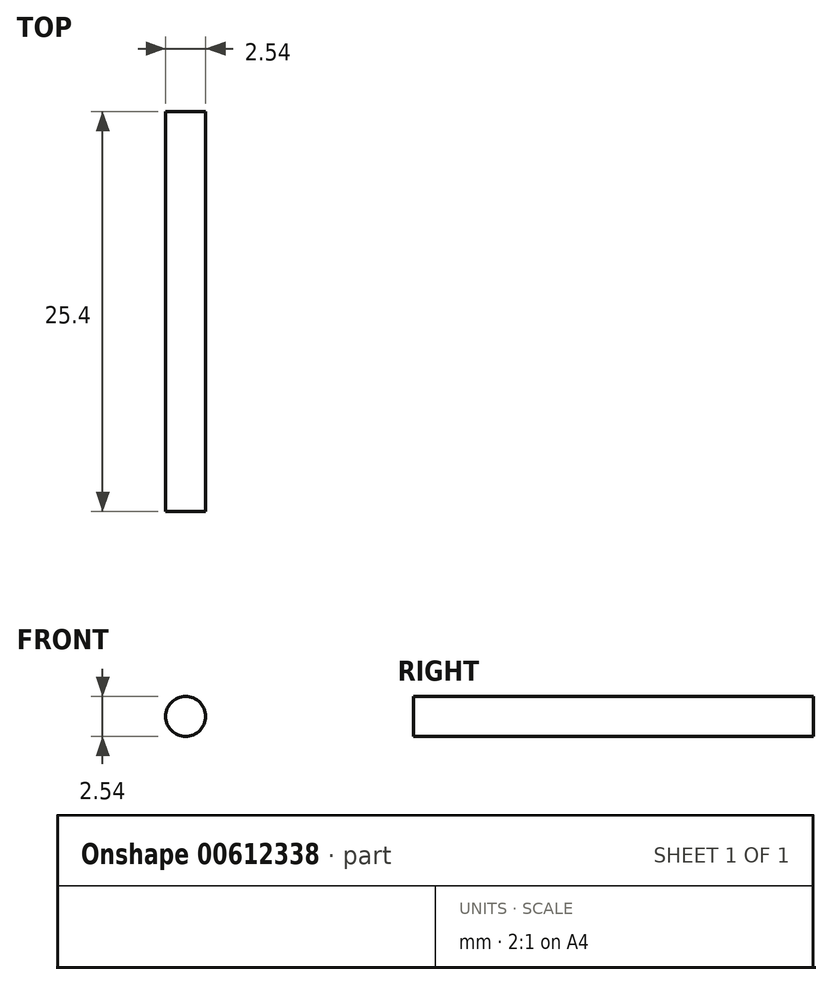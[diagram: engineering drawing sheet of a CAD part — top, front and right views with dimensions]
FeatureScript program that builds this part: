
annotation { "Feature Type Name" : "Feature", "Feature Type Description" : "" }
export const myFeature = defineFeature(function(context is Context, id is Id, definition is map)
    precondition{}
    {
        {
            var Q0;
            Q0=qCreatedBy(makeId("Front.planeOp"),FACE);
            var sketch = newSketch(context, id + "F0", { "sketchPlane" : qUnion([Q0])});
            skCircle(sketch, "E0", {"center": v(0, 0) * mm, "radius": 1.27 * mm});
            skSolve(sketch);
        }
        {
            var Q0;
            Q0=makeQuery(id+"F0.imprint","IMPRINT",FACE,{"disambiguationData":[TD([[makeQuery(id+"F0.imprint","IMPRINT",EDGE,{"derivedFrom":sQuery(id+"F0.wireOp",EDGE,"E0")}),1.0]])]});
            extrude(context, id + "F1", {"entities" : qUnion([Q0]), "depth" : 25.4 * mm, "offsetDistance" : 25.4 * mm});
        }
    });
